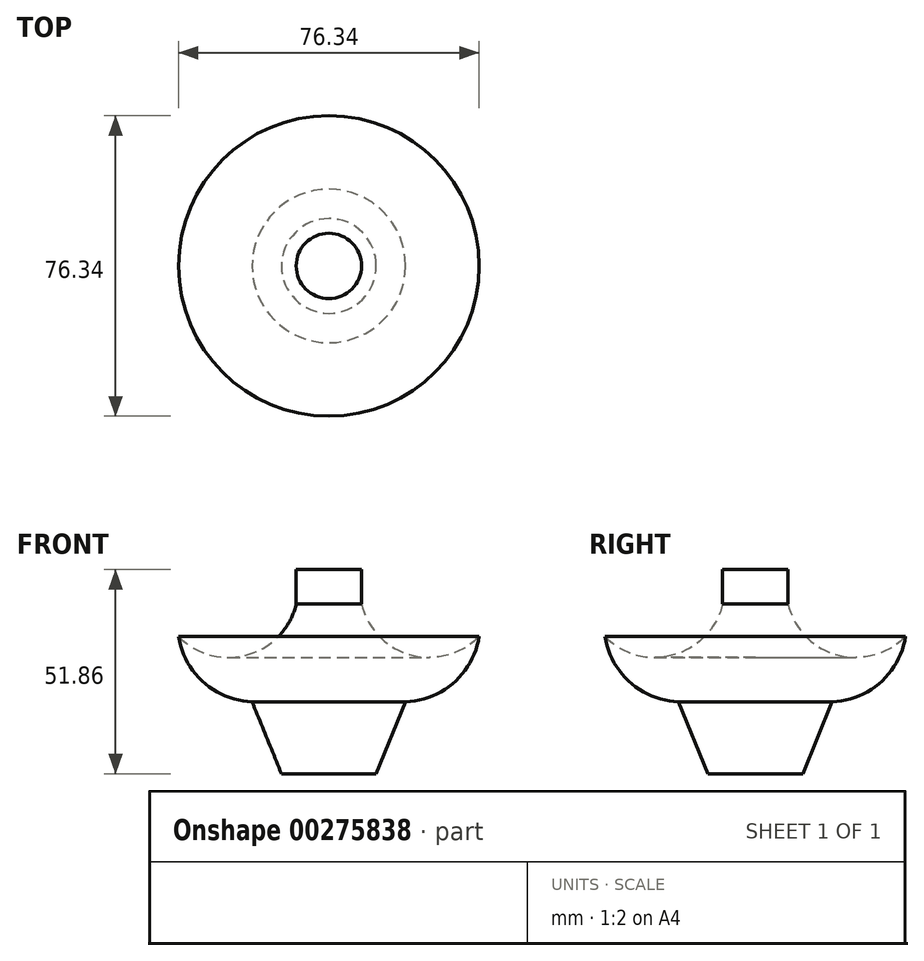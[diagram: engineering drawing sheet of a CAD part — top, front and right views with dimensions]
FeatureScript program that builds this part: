
annotation { "Feature Type Name" : "Feature", "Feature Type Description" : "" }
export const myFeature = defineFeature(function(context is Context, id is Id, definition is map)
    precondition{}
    {
        {
            var Q0;
            Q0=qCreatedBy(makeId("Front.planeOp"),FACE);
            var sketch = newSketch(context, id + "F0", { "sketchPlane" : qUnion([Q0])});
            skLineSegment(sketch, "E0", {"start": v(0, 0) * mm, "end": v(12.03, 0) * mm});
            skLineSegment(sketch, "E1", {"start": v(12.03, 0) * mm, "end": v(19.5, 18.26) * mm});
            skArc(sketch, "E2", {"start": v(19.5, 18.26) * mm, "mid": v(31.8, 23.21) * mm, "end": v(38.17, 34.85) * mm});
            skArc(sketch, "E3", {"start": v(8.3, 43.15) * mm, "mid": v(20.79, 30.2) * mm, "end": v(38.17, 34.85) * mm});
            skLineSegment(sketch, "E4", {"start": v(8.3, 43.15) * mm, "end": v(8.3, 51.86) * mm});
            skLineSegment(sketch, "E5", {"start": v(8.3, 51.86) * mm, "end": v(0, 51.86) * mm});
            skLineSegment(sketch, "E6", {"start": v(0, 0) * mm, "end": v(0, 51.86) * mm});
            skSolve(sketch);
        }
        {
            var Q0;
            Q0=makeQuery(id+"F0.imprint","IMPRINT",FACE,{"disambiguationData":[TD([[makeQuery(id+"F0.imprint","IMPRINT",EDGE,{"derivedFrom":sQuery(id+"F0.wireOp",EDGE,"E0")}),1.0]])]});
            var Q1;
            Q1=sQuery(id+"F0.wireOp",EDGE,"E6");
            revolve(context, id + "F1", {"entities" : qUnion([Q0]), "axis" : qUnion([Q1]), "revolveType" : RevolveType.FULL});
        }
    });
